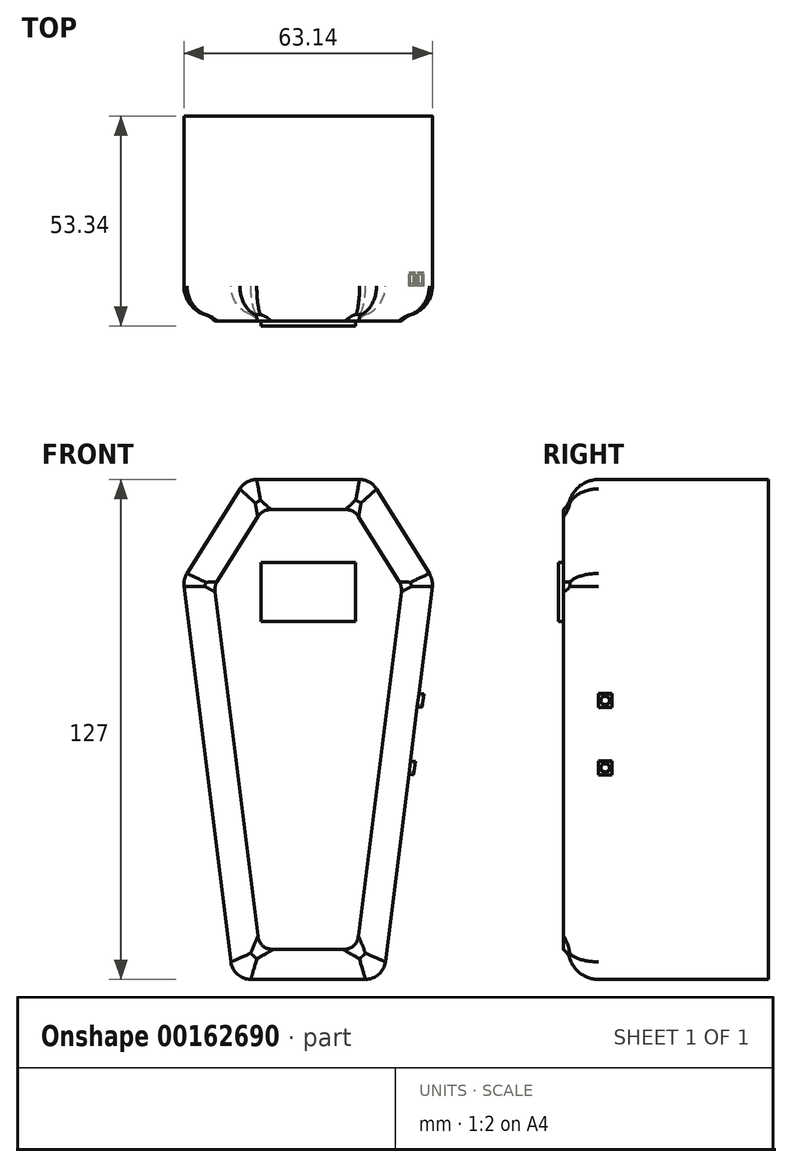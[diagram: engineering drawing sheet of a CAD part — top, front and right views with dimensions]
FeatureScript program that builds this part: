
annotation { "Feature Type Name" : "Feature", "Feature Type Description" : "" }
export const myFeature = defineFeature(function(context is Context, id is Id, definition is map)
    precondition{}
    {
        {
            var Q0;
            Q0=qCreatedBy(makeId("Front.planeOp"),FACE);
            var sketch = newSketch(context, id + "F0", { "sketchPlane" : qUnion([Q0])});
            skLineSegment(sketch, "E0", {"start": v(0, -76.2) * mm, "end": v(-19.05, -76.2) * mm, "construction": true});
            skLineSegment(sketch, "E1", {"start": v(0, -76.2) * mm, "end": v(19.05, -76.2) * mm, "construction": true});
            skLineSegment(sketch, "E2", {"start": v(0, 50.8) * mm, "end": v(-15.88, 50.8) * mm});
            skPoint(sketch, "E2.endSnap0", {"position": v(-15.88, 25.4) * mm});
            skLineSegment(sketch, "E3", {"start": v(0, 50.8) * mm, "end": v(15.88, 50.8) * mm});
            skPoint(sketch, "E3.endSnap0", {"position": v(15.88, 25.4) * mm});
            skLineSegment(sketch, "E4", {"start": v(-15.88, 50.8) * mm, "end": v(-31.75, 25.4) * mm});
            skLineSegment(sketch, "E5", {"start": v(15.88, 50.8) * mm, "end": v(31.75, 25.4) * mm});
            skLineSegment(sketch, "E6", {"start": v(-31.75, 25.4) * mm, "end": v(-19.05, -76.2) * mm});
            skLineSegment(sketch, "E7", {"start": v(31.75, 25.4) * mm, "end": v(19.05, -76.2) * mm});
            skLineSegment(sketch, "E8", {"start": v(-19.05, -76.2) * mm, "end": v(19.05, -76.2) * mm});
            skPoint(sketch, "E9.start.orphan", {"position": v(0, 25.4) * mm});
            skPoint(sketch, "E10.start.orphan", {"position": v(0, 0) * mm});
            skSolve(sketch);
        }
        {
            var Q0;
            Q0=makeQuery(id+"F0.imprint","IMPRINT",FACE,{"disambiguationData":[TD([[makeQuery(id+"F0.imprint","IMPRINT",EDGE,{"derivedFrom":sQuery(id+"F0.wireOp",EDGE,"E2")}),1.0]])]});
            extrude(context, id + "F1", {"entities" : qUnion([Q0]), "depth" : 50.8 * mm});
        }
        {
            var Q0;
            Q0=makeQuery(id+"F1.opExtrude","CAP_EDGE",EDGE,{"disambiguationData":[OSD([sQuery(id+"F0.wireOp",EDGE,"E2"),sQuery(id+"F0.wireOp",EDGE,"E3")])],"isStart":false});
            var Q1;
            Q1=makeQuery(id+"F1.opExtrude","CAP_FACE",FACE,{"disambiguationData":[OSD([sQuery(id+"F0.wireOp",EDGE,"E2"),sQuery(id+"F0.wireOp",EDGE,"E3"),sQuery(id+"F0.wireOp",EDGE,"E4"),sQuery(id+"F0.wireOp",EDGE,"E5"),sQuery(id+"F0.wireOp",EDGE,"E6"),sQuery(id+"F0.wireOp",EDGE,"E7"),sQuery(id+"F0.wireOp",EDGE,"E8")])],"isStart":false});
            var Q2;
            Q2=makeQuery(id+"F1.opExtrude","CAP_EDGE",EDGE,{"disambiguationData":[OSD([sQuery(id+"F0.wireOp",EDGE,"E4")])],"isStart":false});
            var Q3;
            Q3=makeQuery(id+"F1.opExtrude","CAP_EDGE",EDGE,{"disambiguationData":[OSD([sQuery(id+"F0.wireOp",EDGE,"E6")])],"isStart":false});
            var Q4;
            Q4=makeQuery(id+"F1.opExtrude","CAP_EDGE",EDGE,{"disambiguationData":[OSD([sQuery(id+"F0.wireOp",EDGE,"E8")])],"isStart":false});
            var Q5;
            Q5=makeQuery(id+"F1.opExtrude","CAP_EDGE",EDGE,{"disambiguationData":[OSD([sQuery(id+"F0.wireOp",EDGE,"E7")])],"isStart":false});
            var Q6;
            Q6=makeQuery(id+"F1.opExtrude","CAP_EDGE",EDGE,{"disambiguationData":[OSD([sQuery(id+"F0.wireOp",EDGE,"E5")])],"isStart":false});
            fillet(context, id + "F2", {"entities" : qUnion([Q0, Q1, Q2, Q3, Q4, Q5, Q6]), "radius" : 7.62 * mm, "tangentPropagation" : true, "allowEdgeOverflow" : false});
        }
        {
            var Q0;
            Q0=makeQuery(id+"F1.opExtrude","CAP_FACE",FACE,{"disambiguationData":[OSD([sQuery(id+"F0.wireOp",EDGE,"E2"),sQuery(id+"F0.wireOp",EDGE,"E3"),sQuery(id+"F0.wireOp",EDGE,"E4"),sQuery(id+"F0.wireOp",EDGE,"E5"),sQuery(id+"F0.wireOp",EDGE,"E6"),sQuery(id+"F0.wireOp",EDGE,"E7"),sQuery(id+"F0.wireOp",EDGE,"E8")])],"isStart":false});
            extrude(context, id + "F3", {"entities" : qUnion([Q0]), "operationType" : NewBodyOperationType.ADD, "depth" : 1.27 * mm});
        }
        {
            var Q0;
            {var subQ0=sQuery(id+"F0.wireOp",EDGE,"E8");var subQ1=sQuery(id+"F0.wireOp",EDGE,"E7");var subQ2=sQuery(id+"F0.wireOp",EDGE,"E6");var subQ3=sQuery(id+"F0.wireOp",EDGE,"E5");var subQ4=sQuery(id+"F0.wireOp",EDGE,"E4");var subQ5=sQuery(id+"F0.wireOp",EDGE,"E3");var subQ6=sQuery(id+"F0.wireOp",EDGE,"E2");var subQ7=makeQuery(id+"F2.opFillet","BLEND_EDGE",EDGE,{"blendedFrom":[makeQuery(id+"F1.opExtrude","CAP_EDGE",EDGE,{"disambiguationData":[OSD([subQ6,subQ5])],"isStart":false}),makeQuery(id+"F1.opExtrude","CAP_FACE",FACE,{"disambiguationData":[OSD([subQ6,subQ5,subQ4,subQ3,subQ2,subQ1,subQ0])],"isStart":false})],"blendedInto":[makeQuery(id+"F1.opExtrude","CAP_FACE",FACE,{"disambiguationData":[OSD([subQ6,subQ5,subQ4,subQ3,subQ2,subQ1,subQ0])],"isStart":false})]});Q0=makeQuery(id+"F3.boolean.opBoolean","MERGE",EDGE,{"derivedFrom":[subQ7,makeQuery(id+"F3.opExtrude","CAP_EDGE",EDGE,{"disambiguationData":[OSD([subQ6,subQ5,subQ4,subQ3,subQ2,subQ1,subQ0]),TDD([subQ7])],"isStart":true})]});}
            var Q1;
            {var subQ0=sQuery(id+"F0.wireOp",EDGE,"E8");var subQ1=sQuery(id+"F0.wireOp",EDGE,"E7");var subQ2=sQuery(id+"F0.wireOp",EDGE,"E6");var subQ3=sQuery(id+"F0.wireOp",EDGE,"E5");var subQ4=sQuery(id+"F0.wireOp",EDGE,"E4");var subQ5=sQuery(id+"F0.wireOp",EDGE,"E3");var subQ6=sQuery(id+"F0.wireOp",EDGE,"E2");var subQ7=makeQuery(id+"F2.opFillet","BLEND_EDGE",EDGE,{"blendedFrom":[makeQuery(id+"F1.opExtrude","CAP_EDGE",EDGE,{"disambiguationData":[OSD([subQ3])],"isStart":false}),makeQuery(id+"F1.opExtrude","CAP_FACE",FACE,{"disambiguationData":[OSD([subQ6,subQ5,subQ4,subQ3,subQ2,subQ1,subQ0])],"isStart":false})],"blendedInto":[makeQuery(id+"F1.opExtrude","CAP_FACE",FACE,{"disambiguationData":[OSD([subQ6,subQ5,subQ4,subQ3,subQ2,subQ1,subQ0])],"isStart":false})]});Q1=makeQuery(id+"F3.boolean.opBoolean","MERGE",EDGE,{"derivedFrom":[subQ7,makeQuery(id+"F3.opExtrude","CAP_EDGE",EDGE,{"disambiguationData":[OSD([subQ6,subQ5,subQ4,subQ3,subQ2,subQ1,subQ0]),TDD([subQ7])],"isStart":true})]});}
            var Q2;
            {var subQ0=sQuery(id+"F0.wireOp",EDGE,"E8");var subQ1=sQuery(id+"F0.wireOp",EDGE,"E7");var subQ2=sQuery(id+"F0.wireOp",EDGE,"E6");var subQ3=sQuery(id+"F0.wireOp",EDGE,"E5");var subQ4=sQuery(id+"F0.wireOp",EDGE,"E4");var subQ5=sQuery(id+"F0.wireOp",EDGE,"E3");var subQ6=sQuery(id+"F0.wireOp",EDGE,"E2");var subQ7=makeQuery(id+"F2.opFillet","BLEND_EDGE",EDGE,{"blendedFrom":[makeQuery(id+"F1.opExtrude","CAP_EDGE",EDGE,{"disambiguationData":[OSD([subQ1])],"isStart":false}),makeQuery(id+"F1.opExtrude","CAP_FACE",FACE,{"disambiguationData":[OSD([subQ6,subQ5,subQ4,subQ3,subQ2,subQ1,subQ0])],"isStart":false})],"blendedInto":[makeQuery(id+"F1.opExtrude","CAP_FACE",FACE,{"disambiguationData":[OSD([subQ6,subQ5,subQ4,subQ3,subQ2,subQ1,subQ0])],"isStart":false})]});Q2=makeQuery(id+"F3.boolean.opBoolean","MERGE",EDGE,{"derivedFrom":[subQ7,makeQuery(id+"F3.opExtrude","CAP_EDGE",EDGE,{"disambiguationData":[OSD([subQ6,subQ5,subQ4,subQ3,subQ2,subQ1,subQ0]),TDD([subQ7])],"isStart":true})]});}
            var Q3;
            {var subQ0=sQuery(id+"F0.wireOp",EDGE,"E8");var subQ1=sQuery(id+"F0.wireOp",EDGE,"E7");var subQ2=sQuery(id+"F0.wireOp",EDGE,"E6");var subQ3=sQuery(id+"F0.wireOp",EDGE,"E5");var subQ4=sQuery(id+"F0.wireOp",EDGE,"E4");var subQ5=sQuery(id+"F0.wireOp",EDGE,"E3");var subQ6=sQuery(id+"F0.wireOp",EDGE,"E2");var subQ7=makeQuery(id+"F2.opFillet","BLEND_EDGE",EDGE,{"blendedFrom":[makeQuery(id+"F1.opExtrude","CAP_EDGE",EDGE,{"disambiguationData":[OSD([subQ4])],"isStart":false}),makeQuery(id+"F1.opExtrude","CAP_FACE",FACE,{"disambiguationData":[OSD([subQ6,subQ5,subQ4,subQ3,subQ2,subQ1,subQ0])],"isStart":false})],"blendedInto":[makeQuery(id+"F1.opExtrude","CAP_FACE",FACE,{"disambiguationData":[OSD([subQ6,subQ5,subQ4,subQ3,subQ2,subQ1,subQ0])],"isStart":false})]});Q3=makeQuery(id+"F3.boolean.opBoolean","MERGE",EDGE,{"derivedFrom":[subQ7,makeQuery(id+"F3.opExtrude","CAP_EDGE",EDGE,{"disambiguationData":[OSD([subQ6,subQ5,subQ4,subQ3,subQ2,subQ1,subQ0]),TDD([subQ7])],"isStart":true})]});}
            var Q4;
            {var subQ0=sQuery(id+"F0.wireOp",EDGE,"E8");var subQ1=sQuery(id+"F0.wireOp",EDGE,"E7");var subQ2=sQuery(id+"F0.wireOp",EDGE,"E6");var subQ3=sQuery(id+"F0.wireOp",EDGE,"E5");var subQ4=sQuery(id+"F0.wireOp",EDGE,"E4");var subQ5=sQuery(id+"F0.wireOp",EDGE,"E3");var subQ6=sQuery(id+"F0.wireOp",EDGE,"E2");var subQ7=makeQuery(id+"F2.opFillet","BLEND_EDGE",EDGE,{"blendedFrom":[makeQuery(id+"F1.opExtrude","CAP_EDGE",EDGE,{"disambiguationData":[OSD([subQ0])],"isStart":false}),makeQuery(id+"F1.opExtrude","CAP_FACE",FACE,{"disambiguationData":[OSD([subQ6,subQ5,subQ4,subQ3,subQ2,subQ1,subQ0])],"isStart":false})],"blendedInto":[makeQuery(id+"F1.opExtrude","CAP_FACE",FACE,{"disambiguationData":[OSD([subQ6,subQ5,subQ4,subQ3,subQ2,subQ1,subQ0])],"isStart":false})]});Q4=makeQuery(id+"F3.boolean.opBoolean","MERGE",EDGE,{"derivedFrom":[subQ7,makeQuery(id+"F3.opExtrude","CAP_EDGE",EDGE,{"disambiguationData":[OSD([subQ6,subQ5,subQ4,subQ3,subQ2,subQ1,subQ0]),TDD([subQ7])],"isStart":true})]});}
            var Q5;
            {var subQ0=sQuery(id+"F0.wireOp",EDGE,"E8");var subQ1=sQuery(id+"F0.wireOp",EDGE,"E7");var subQ2=sQuery(id+"F0.wireOp",EDGE,"E6");var subQ3=sQuery(id+"F0.wireOp",EDGE,"E5");var subQ4=sQuery(id+"F0.wireOp",EDGE,"E4");var subQ5=sQuery(id+"F0.wireOp",EDGE,"E3");var subQ6=sQuery(id+"F0.wireOp",EDGE,"E2");var subQ7=makeQuery(id+"F2.opFillet","BLEND_EDGE",EDGE,{"blendedFrom":[makeQuery(id+"F1.opExtrude","CAP_EDGE",EDGE,{"disambiguationData":[OSD([subQ2])],"isStart":false}),makeQuery(id+"F1.opExtrude","CAP_FACE",FACE,{"disambiguationData":[OSD([subQ6,subQ5,subQ4,subQ3,subQ2,subQ1,subQ0])],"isStart":false})],"blendedInto":[makeQuery(id+"F1.opExtrude","CAP_FACE",FACE,{"disambiguationData":[OSD([subQ6,subQ5,subQ4,subQ3,subQ2,subQ1,subQ0])],"isStart":false})]});Q5=makeQuery(id+"F3.boolean.opBoolean","MERGE",EDGE,{"derivedFrom":[subQ7,makeQuery(id+"F3.opExtrude","CAP_EDGE",EDGE,{"disambiguationData":[OSD([subQ6,subQ5,subQ4,subQ3,subQ2,subQ1,subQ0]),TDD([subQ7])],"isStart":true})]});}
            fillet(context, id + "F4", {"entities" : qUnion([Q0, Q1, Q2, Q3, Q4, Q5]), "radius" : 5.08 * mm, "tangentPropagation" : true, "allowEdgeOverflow" : false});
        }
        {
            var Q0;
            Q0=makeQuery(id+"F1.opExtrude","SWEPT_EDGE",EDGE,{"disambiguationData":[OSD([sQuery(id+"F0.wireOp",EDGE,"E3"),sQuery(id+"F0.wireOp",EDGE,"E5")])]});
            var Q1;
            Q1=makeQuery(id+"F1.opExtrude","SWEPT_EDGE",EDGE,{"disambiguationData":[OSD([sQuery(id+"F0.wireOp",EDGE,"E5"),sQuery(id+"F0.wireOp",EDGE,"E7")])]});
            var Q2;
            Q2=makeQuery(id+"F1.opExtrude","SWEPT_EDGE",EDGE,{"disambiguationData":[OSD([sQuery(id+"F0.wireOp",EDGE,"E7"),sQuery(id+"F0.wireOp",EDGE,"E8")])]});
            var Q3;
            Q3=makeQuery(id+"F1.opExtrude","SWEPT_EDGE",EDGE,{"disambiguationData":[OSD([sQuery(id+"F0.wireOp",EDGE,"E6"),sQuery(id+"F0.wireOp",EDGE,"E8")])]});
            var Q4;
            Q4=makeQuery(id+"F1.opExtrude","SWEPT_EDGE",EDGE,{"disambiguationData":[OSD([sQuery(id+"F0.wireOp",EDGE,"E4"),sQuery(id+"F0.wireOp",EDGE,"E6")])]});
            var Q5;
            Q5=makeQuery(id+"F1.opExtrude","SWEPT_EDGE",EDGE,{"disambiguationData":[OSD([sQuery(id+"F0.wireOp",EDGE,"E2"),sQuery(id+"F0.wireOp",EDGE,"E4")])]});
            fillet(context, id + "F5", {"entities" : qUnion([Q0, Q1, Q2, Q3, Q4, Q5]), "radius" : 5.08 * mm, "tangentPropagation" : true, "allowEdgeOverflow" : false});
        }
        {
            var Q0;
            Q0=makeQuery(id+"F3.opExtrude","CAP_FACE",FACE,{"disambiguationData":[OSD([sQuery(id+"F0.wireOp",EDGE,"E2"),sQuery(id+"F0.wireOp",EDGE,"E3"),sQuery(id+"F0.wireOp",EDGE,"E4"),sQuery(id+"F0.wireOp",EDGE,"E5"),sQuery(id+"F0.wireOp",EDGE,"E6"),sQuery(id+"F0.wireOp",EDGE,"E7"),sQuery(id+"F0.wireOp",EDGE,"E8")])],"isStart":false});
            var sketch = newSketch(context, id + "F6", { "sketchPlane" : qUnion([Q0])});
            skLineSegment(sketch, "E11.bottom", {"start": v(-12.02, 29.75) * mm, "end": v(12.02, 29.75) * mm});
            skLineSegment(sketch, "E11.top", {"start": v(-12.02, 14.77) * mm, "end": v(12.02, 14.77) * mm});
            skLineSegment(sketch, "E11.left", {"start": v(-12.02, 29.75) * mm, "end": v(-12.02, 14.77) * mm});
            skLineSegment(sketch, "E11.right", {"start": v(12.02, 29.75) * mm, "end": v(12.02, 14.77) * mm});
            skPoint(sketch, "E11.middle", {"position": v(0, 22.26) * mm});
            skPoint(sketch, "E11.middle.positionSnap0", {"position": v(0, 43.18) * mm});
            skPoint(sketch, "E11.centerSnap0", {"position": v(0, 43.18) * mm});
            skSolve(sketch);
        }
        {
            var Q0;
            Q0 = qSketchRegion(id + "F6", true);
            extrude(context, id + "F7", {"entities" : qUnion([Q0]), "operationType" : NewBodyOperationType.ADD, "depth" : 1.27 * mm});
        }
        {
            var Q0;
            Q0=makeQuery(id+"F1.opExtrude","SWEPT_FACE",FACE,{"disambiguationData":[OSD([sQuery(id+"F0.wireOp",EDGE,"E7")])]});
            var sketch = newSketch(context, id + "F8", { "sketchPlane" : qUnion([Q0])});
            skLineSegment(sketch, "E12.bottom", {"start": v(-43.18, -20.71) * mm, "end": v(-39.72, -20.71) * mm});
            skLineSegment(sketch, "E12.top", {"start": v(-43.18, -17.26) * mm, "end": v(-39.72, -17.26) * mm});
            skLineSegment(sketch, "E12.left", {"start": v(-43.18, -20.71) * mm, "end": v(-43.18, -17.26) * mm});
            skLineSegment(sketch, "E12.right", {"start": v(-39.72, -20.71) * mm, "end": v(-39.72, -17.26) * mm});
            skLineSegment(sketch, "E13.bottom", {"start": v(-43.18, 0) * mm, "end": v(-39.72, 0) * mm});
            skLineSegment(sketch, "E13.top", {"start": v(-43.18, -3.46) * mm, "end": v(-39.72, -3.46) * mm});
            skLineSegment(sketch, "E13.left", {"start": v(-43.18, 0) * mm, "end": v(-43.18, -3.46) * mm});
            skLineSegment(sketch, "E13.right", {"start": v(-39.72, 0) * mm, "end": v(-39.72, -3.46) * mm});
            skLineSegment(sketch, "E14", {"start": v(-41.45, 0) * mm, "end": v(-41.45, -20.71) * mm, "construction": true});
            skLineSegment(sketch, "E15", {"start": v(-39.72, -1.73) * mm, "end": v(-43.18, -1.73) * mm, "construction": true});
            skLineSegment(sketch, "E16", {"start": v(-39.72, -18.99) * mm, "end": v(-43.18, -18.99) * mm, "construction": true});
            skCircle(sketch, "E17", {"center": v(-41.45, -1.73) * mm, "radius": 1.13 * mm});
            skCircle(sketch, "E18", {"center": v(-41.45, -18.99) * mm, "radius": 1.13 * mm});
            skSolve(sketch);
        }
        {
            var Q0;
            Q0 = qSketchRegion(id + "F8", true);
            extrude(context, id + "F9", {"entities" : qUnion([Q0]), "operationType" : NewBodyOperationType.ADD, "depth" : 1.27 * mm});
        }
    });
